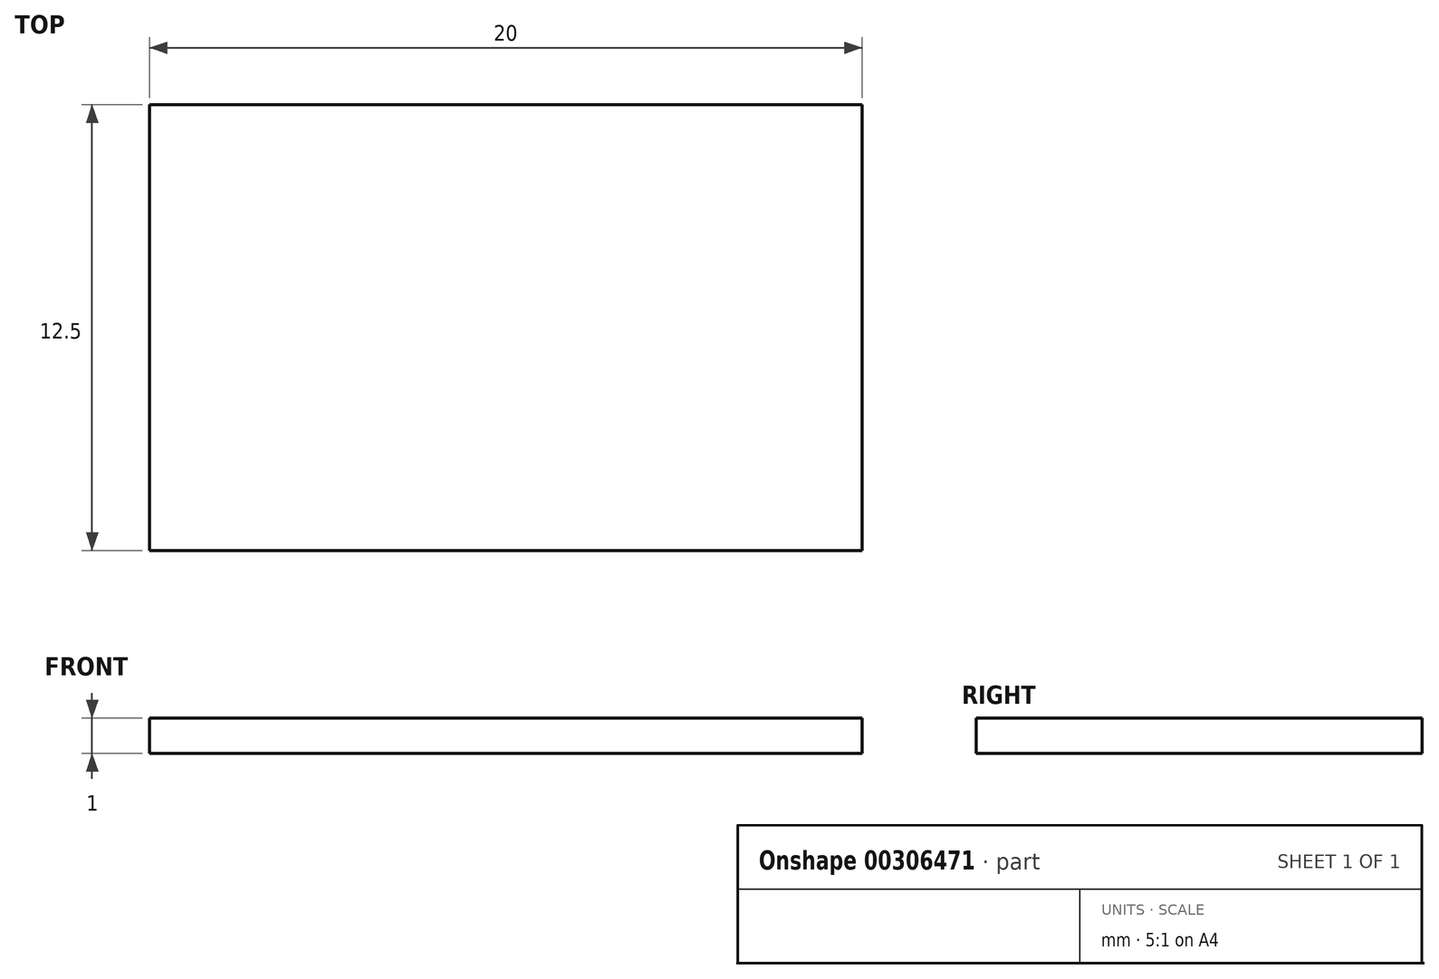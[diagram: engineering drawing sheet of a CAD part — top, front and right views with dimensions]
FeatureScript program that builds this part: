
annotation { "Feature Type Name" : "Feature", "Feature Type Description" : "" }
export const myFeature = defineFeature(function(context is Context, id is Id, definition is map)
    precondition{}
    {
        {
            var Q0;
            Q0=qCreatedBy(makeId("Top.planeOp"),FACE);
            var sketch = newSketch(context, id + "F0", { "sketchPlane" : qUnion([Q0])});
            skLineSegment(sketch, "E0.bottom", {"start": v(0, 0) * mm, "end": v(-40, 0) * mm});
            skLineSegment(sketch, "E0.top", {"start": v(0, 25) * mm, "end": v(-40, 25) * mm});
            skLineSegment(sketch, "E0.left", {"start": v(0, 0) * mm, "end": v(0, 25) * mm});
            skLineSegment(sketch, "E0.right", {"start": v(-40, 0) * mm, "end": v(-40, 25) * mm});
            skSolve(sketch);
        }
        {
            var Q0;
            Q0=makeQuery(id+"F0.imprint","IMPRINT",FACE,{"disambiguationData":[TD([[makeQuery(id+"F0.imprint","IMPRINT",EDGE,{"derivedFrom":sQuery(id+"F0.wireOp",EDGE,"E0.bottom")}),-1.0]])]});
            extrude(context, id + "F1", {"entities" : qUnion([Q0]), "depth" : 2 * mm});
        }
        {
            var Q0;
            Q0=makeQuery(id+"F1.opExtrude","SWEPT_BODY",BODY,{"disambiguationData":[OSD([sQuery(id+"F0.wireOp",EDGE,"E0.bottom"),sQuery(id+"F0.wireOp",EDGE,"E0.top"),sQuery(id+"F0.wireOp",EDGE,"E0.left"),sQuery(id+"F0.wireOp",EDGE,"E0.right")])]});
            var Q1;
            Q1=qCreatedBy(makeId("Origin.pointOp"),VERTEX);
            var Q2;
            Q2=qCreatedBy(makeId("Origin.pointOp"),VERTEX);
            transform(context, id + "F2", {"entities" : qUnion([Q0]), "transformType" : TransformType.SCALE_UNIFORMLY, "scale" : 0.5, "scalePoint" : qUnion([Q2]), "makeCopy" : false});
        }
    });
